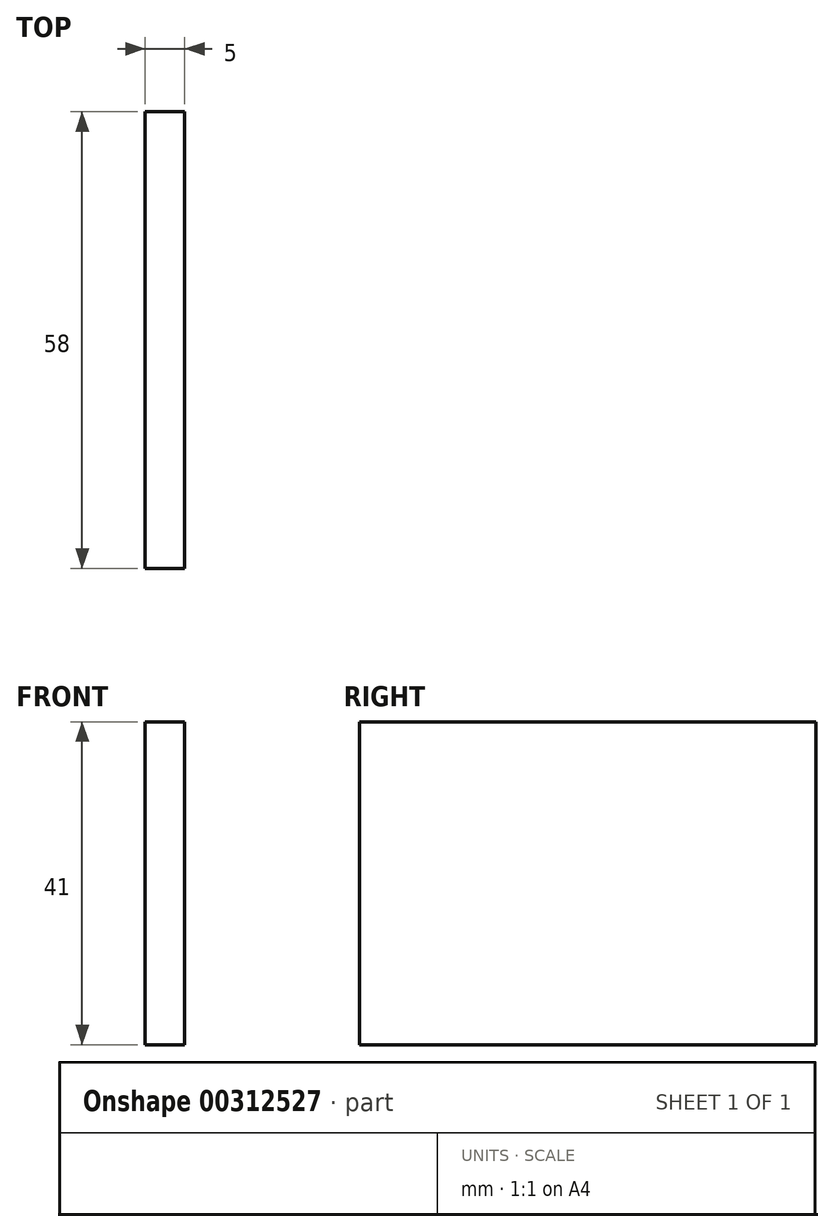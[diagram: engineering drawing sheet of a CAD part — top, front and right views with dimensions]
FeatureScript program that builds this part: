
annotation { "Feature Type Name" : "Feature", "Feature Type Description" : "" }
export const myFeature = defineFeature(function(context is Context, id is Id, definition is map)
    precondition{}
    {
        {
            var Q0;
            Q0=qCreatedBy(makeId("Front.planeOp"),FACE);
            var sketch = newSketch(context, id + "F0", { "sketchPlane" : qUnion([Q0])});
            skLineSegment(sketch, "E0.bottom", {"start": v(2.5, 20.5) * mm, "end": v(-2.5, 20.5) * mm});
            skLineSegment(sketch, "E0.top", {"start": v(2.5, -20.5) * mm, "end": v(-2.5, -20.5) * mm});
            skLineSegment(sketch, "E0.left", {"start": v(2.5, 20.5) * mm, "end": v(2.5, -20.5) * mm});
            skLineSegment(sketch, "E0.right", {"start": v(-2.5, 20.5) * mm, "end": v(-2.5, -20.5) * mm});
            skPoint(sketch, "E0.middle", {"position": v(0, 0) * mm});
            skSolve(sketch);
        }
        {
            var Q0;
            Q0=makeQuery(id+"F0.imprint","IMPRINT",FACE,{"disambiguationData":[TD([[makeQuery(id+"F0.imprint","IMPRINT",EDGE,{"derivedFrom":sQuery(id+"F0.wireOp",EDGE,"E0.bottom")}),1.0]])]});
            extrude(context, id + "F1", {"entities" : qUnion([Q0]), "depth" : 58 * mm});
        }
    });
